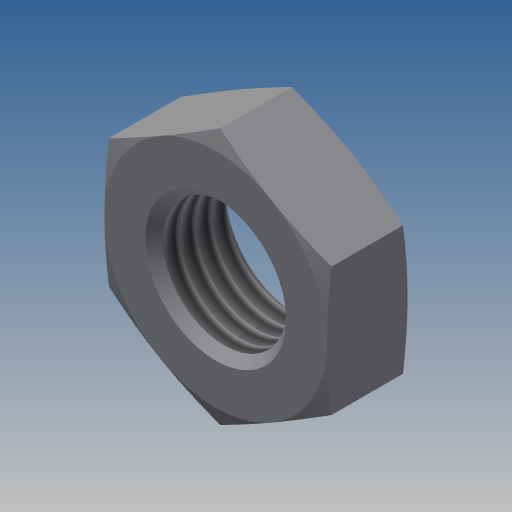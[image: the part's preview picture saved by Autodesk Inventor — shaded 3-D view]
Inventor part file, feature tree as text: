
AUTODESK INVENTOR PART (.ipt)
format: ipt  version: 2020 (Build 240168000, 168)  size: 186,880 bytes
history: native  units: in
note: dims shown in document units (in); Inventor stores cm internally (conversion verified against a paired STEP export)
features: other x70, sketch x3, revolve x2, extrude x1, thread x1
ambient origin geometry x8: Origin, YZ Plane, XZ Plane, XY Plane, X Axis, Y Axis, Z Axis, Center Point
bodies: Solid1 (feature_tree)
feature tree (77):
  sketch  "Sketch_8"  dims[d0=360.0deg d1=0.25in d2=0.0in]
  sketch  "Sketch_10"  dims[d3=360.0deg d4=0.1959in d5=0.0in]
  revolve  "Revolution1"  [1 undecoded]
  extrude  "Extrusion1"  Depth=0.1959in TaperAngle=0.0deg
  revolve  "Revolution2"  [1 undecoded]
  thread  "Thread1"  [1 undecoded]
  other  "NUT_XY"
  other  "NUT_YZ"
  other  "NUT_ZX"
  other  "NUT_X"
  other  "NUT_Y"
  other  "NUT_Z"
  other  "NUT_Center"
  other  "a1_XY"
  other  "a1_YZ"
  other  "a1_ZX"
  other  "a1_X"
  other  "a1_Y"
  other  "a1_Z"
  other  "a1_Center"
  other  "a2_XY"
  other  "a2_YZ"
  other  "a2_ZX"
  other  "a2_X"
  other  "a2_Y"
  other  "a2_Z"
  other  "a2_Center"
  other  "b1_XY"
  other  "b1_YZ"
  other  "b1_ZX"
  other  "b1_X"
  other  "b1_Y"
  other  "b1_Z"
  other  "b1_Center"
  other  "b2_XY"
  other  "b2_YZ"
  other  "b2_ZX"
  other  "b2_X"
  other  "b2_Y"
  other  "b2_Z"
  other  "b2_Center"
  other  "e_XY"
  other  "e_YZ"
  other  "e_ZX"
  other  "e_X"
  other  "e_Y"
  other  "e_Z"
  other  "e_Center"
  other  "ol1_XY"
  other  "ol1_YZ"
  other  "ol1_ZX"
  other  "ol1_X"
  other  "ol1_Y"
  other  "ol1_Z"
  other  "ol1_Center"
  other  "ol2_XY"
  other  "ol2_YZ"
  other  "ol2_ZX"
  other  "ol2_X"
  other  "ol2_Y"
  other  "ol2_Z"
  other  "ol2_Center"
  other  "th1_XY"
  other  "th1_YZ"
  other  "th1_ZX"
  other  "th1_X"
  other  "th1_Y"
  other  "th1_Z"
  other  "th1_Center"
  other  "th2_XY"
  other  "th2_YZ"
  other  "th2_ZX"
  other  "th2_X"
  other  "th2_Y"
  other  "th2_Z"
  other  "th2_Center"
  sketch  "Sketch_11"  dims[d6=0.0in d7=0.0in d8=0.0in]
note: 3 required parameter values undecoded (feature->parameter linkage not recoverable at this tier; creation-order binding heuristic only, values carry confidence <= 0.55)